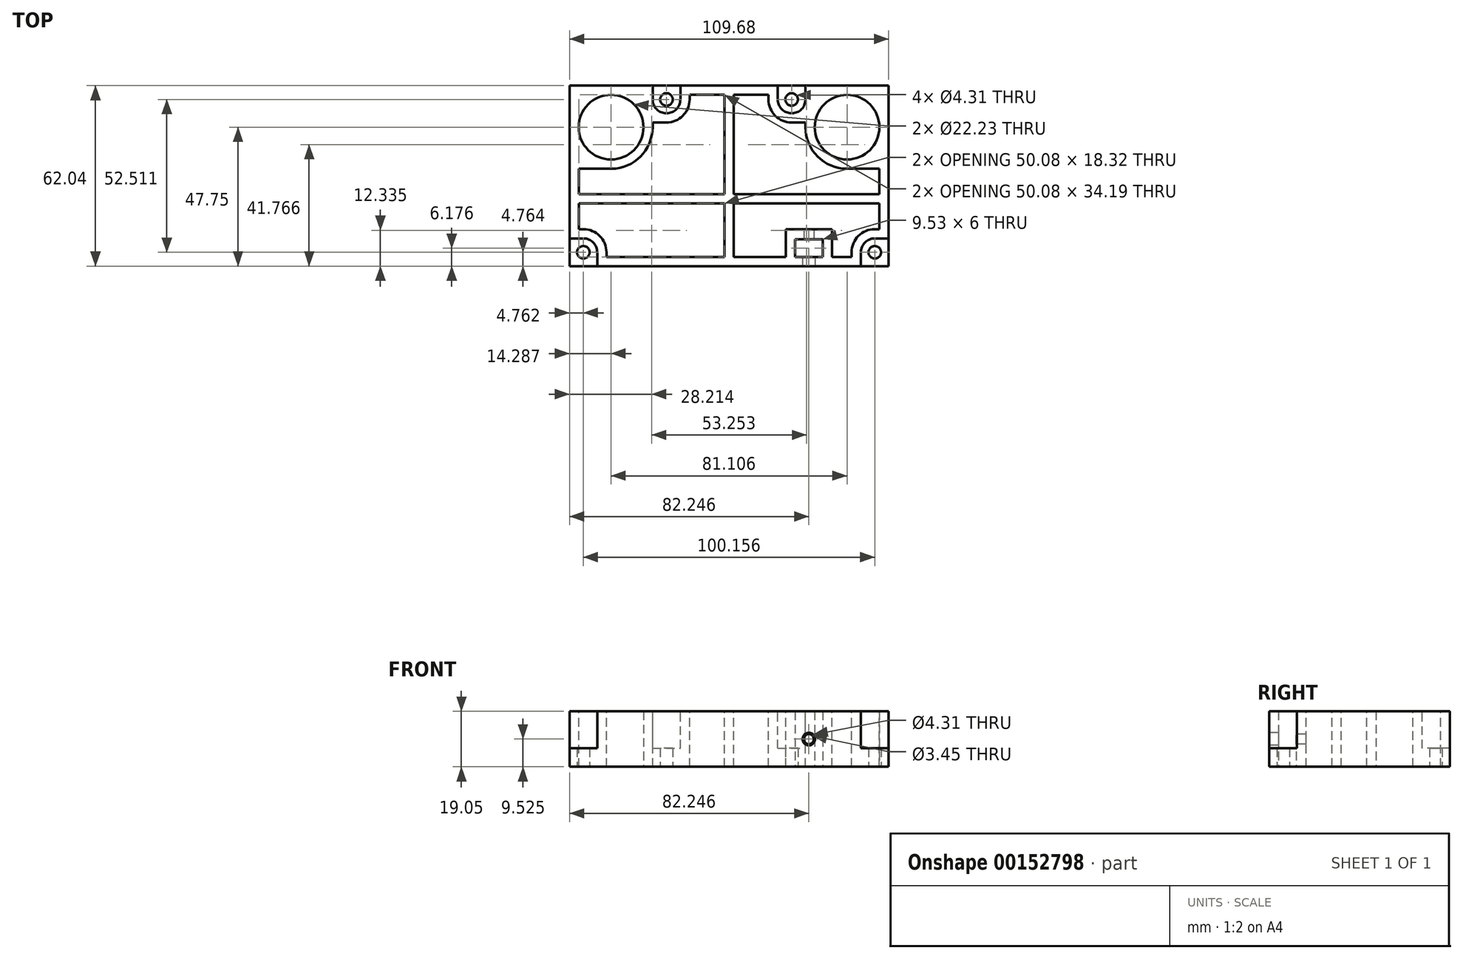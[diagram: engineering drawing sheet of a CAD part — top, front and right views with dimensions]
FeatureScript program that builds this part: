
annotation { "Feature Type Name" : "Feature", "Feature Type Description" : "" }
export const myFeature = defineFeature(function(context is Context, id is Id, definition is map)
    precondition{}
    {
        {
            var Q0;
            Q0=qCreatedBy(makeId("Top.planeOp"),FACE);
            var sketch = newSketch(context, id + "F0", { "sketchPlane" : qUnion([Q0])});
            skLineSegment(sketch, "E0.bottom", {"start": v(-40.55, 0) * mm, "end": v(40.55, 0) * mm, "construction": true});
            skPoint(sketch, "E0.middle", {"position": v(0, 0) * mm});
            skLineSegment(sketch, "E1", {"start": v(-40.55, 0) * mm, "end": v(-40.55, 14.29) * mm, "construction": true});
            skLineSegment(sketch, "E2", {"start": v(-40.55, 0) * mm, "end": v(-54.84, 0) * mm, "construction": true});
            skCircle(sketch, "E3", {"center": v(-40.55, 0) * mm, "radius": 11.11 * mm});
            skCircle(sketch, "E4", {"center": v(40.55, 0) * mm, "radius": 11.11 * mm});
            skLineSegment(sketch, "E5.bottom", {"start": v(-54.84, 14.29) * mm, "end": v(54.84, 14.29) * mm});
            skLineSegment(sketch, "E5.top", {"start": v(-54.84, -47.75) * mm, "end": v(54.84, -47.75) * mm});
            skLineSegment(sketch, "E5.left", {"start": v(-54.84, 14.29) * mm, "end": v(-54.84, -47.75) * mm});
            skLineSegment(sketch, "E5.right", {"start": v(54.84, 14.29) * mm, "end": v(54.84, -47.75) * mm});
            skLineSegment(sketch, "E6", {"start": v(0, 0) * mm, "end": v(0, -41.57) * mm, "construction": true});
            skLineSegment(sketch, "E7", {"start": v(0, -41.57) * mm, "end": v(22.64, -41.57) * mm, "construction": true});
            skLineSegment(sketch, "E8.bottom", {"start": v(22.64, -38.57) * mm, "end": v(32.17, -38.57) * mm});
            skLineSegment(sketch, "E8.top", {"start": v(22.64, -44.57) * mm, "end": v(32.17, -44.57) * mm});
            skLineSegment(sketch, "E8.left", {"start": v(22.64, -38.57) * mm, "end": v(22.64, -44.57) * mm});
            skLineSegment(sketch, "E8.right", {"start": v(32.17, -38.57) * mm, "end": v(32.17, -44.57) * mm});
            skLineSegment(sketch, "E9", {"start": v(0, -41.57) * mm, "end": v(0, -47.75) * mm, "construction": true});
            skLineSegment(sketch, "E10", {"start": v(0, 0) * mm, "end": v(0, 9.53) * mm, "construction": true});
            skLineSegment(sketch, "E11", {"start": v(-21.5, 9.53) * mm, "end": v(21.5, 9.53) * mm, "construction": true});
            skLineSegment(sketch, "E12", {"start": v(-50.08, -47.75) * mm, "end": v(-50.08, -42.99) * mm, "construction": true});
            skLineSegment(sketch, "E13", {"start": v(-50.08, -42.99) * mm, "end": v(-54.84, -42.99) * mm, "construction": true});
            skLineSegment(sketch, "E14", {"start": v(54.84, -42.99) * mm, "end": v(50.08, -42.99) * mm, "construction": true});
            skCircle(sketch, "E15", {"center": v(-50.08, -42.99) * mm, "radius": 2.15 * mm});
            skCircle(sketch, "E16", {"center": v(50.08, -42.99) * mm, "radius": 2.15 * mm});
            skCircle(sketch, "E17", {"center": v(-21.5, 9.53) * mm, "radius": 2.15 * mm});
            skCircle(sketch, "E18", {"center": v(21.5, 9.53) * mm, "radius": 2.15 * mm});
            skSolve(sketch);
        }
        {
            var Q0;
            Q0 = qSketchRegion(id + "F0", true);
            extrude(context, id + "F1", {"entities" : qUnion([Q0]), "depth" : 19.05 * mm});
        }
        {
            var Q0;
            Q0=makeQuery(id+"F1.opExtrude","CAP_FACE",FACE,{"disambiguationData":[OSD([sQuery(id+"F0.wireOp",EDGE,"E3"),sQuery(id+"F0.wireOp",EDGE,"E4"),sQuery(id+"F0.wireOp",EDGE,"E5.bottom"),sQuery(id+"F0.wireOp",EDGE,"E5.top"),sQuery(id+"F0.wireOp",EDGE,"E5.left"),sQuery(id+"F0.wireOp",EDGE,"E5.right"),sQuery(id+"F0.wireOp",EDGE,"E8.bottom"),sQuery(id+"F0.wireOp",EDGE,"E8.top"),sQuery(id+"F0.wireOp",EDGE,"E8.left"),sQuery(id+"F0.wireOp",EDGE,"E8.right"),sQuery(id+"F0.wireOp",EDGE,"E15"),sQuery(id+"F0.wireOp",EDGE,"E16"),sQuery(id+"F0.wireOp",EDGE,"E17"),sQuery(id+"F0.wireOp",EDGE,"E18")])],"isStart":false});
            var sketch = newSketch(context, id + "F2", { "sketchPlane" : qUnion([Q0])});
            skLineSegment(sketch, "E19.bottom", {"start": v(-26.27, 14.29) * mm, "end": v(-16.74, 14.29) * mm});
            skLineSegment(sketch, "E19.top", {"start": v(-26.27, 4.76) * mm, "end": v(-16.74, 4.76) * mm});
            skLineSegment(sketch, "E19.left", {"start": v(-26.27, 14.29) * mm, "end": v(-26.27, 4.76) * mm});
            skLineSegment(sketch, "E19.right", {"start": v(-16.74, 14.29) * mm, "end": v(-16.74, 4.76) * mm});
            skPoint(sketch, "E19.middle", {"position": v(-21.5, 9.53) * mm});
            skLineSegment(sketch, "E20.bottom", {"start": v(26.27, 14.29) * mm, "end": v(16.74, 14.29) * mm});
            skLineSegment(sketch, "E20.top", {"start": v(26.27, 4.76) * mm, "end": v(16.74, 4.76) * mm});
            skLineSegment(sketch, "E20.left", {"start": v(26.27, 14.29) * mm, "end": v(26.27, 4.76) * mm});
            skLineSegment(sketch, "E20.right", {"start": v(16.74, 14.29) * mm, "end": v(16.74, 4.76) * mm});
            skPoint(sketch, "E20.middle", {"position": v(21.5, 9.53) * mm});
            skLineSegment(sketch, "E21.bottom", {"start": v(54.84, -47.75) * mm, "end": v(45.32, -47.75) * mm});
            skLineSegment(sketch, "E21.top", {"start": v(54.84, -38.22) * mm, "end": v(45.32, -38.22) * mm});
            skLineSegment(sketch, "E21.left", {"start": v(54.84, -47.75) * mm, "end": v(54.84, -38.22) * mm});
            skLineSegment(sketch, "E21.right", {"start": v(45.32, -47.75) * mm, "end": v(45.32, -38.22) * mm});
            skPoint(sketch, "E21.middle", {"position": v(50.08, -42.99) * mm});
            skLineSegment(sketch, "E22.bottom", {"start": v(-54.84, -47.75) * mm, "end": v(-45.32, -47.75) * mm});
            skLineSegment(sketch, "E22.top", {"start": v(-54.84, -38.22) * mm, "end": v(-45.32, -38.22) * mm});
            skLineSegment(sketch, "E22.left", {"start": v(-54.84, -47.75) * mm, "end": v(-54.84, -38.22) * mm});
            skLineSegment(sketch, "E22.right", {"start": v(-45.32, -47.75) * mm, "end": v(-45.32, -38.22) * mm});
            skPoint(sketch, "E22.middle", {"position": v(-50.08, -42.99) * mm});
            skSolve(sketch);
        }
        {
            var Q0;
            Q0 = qSketchRegion(id + "F2", true);
            extrude(context, id + "F3", {"entities" : qUnion([Q0]), "operationType" : NewBodyOperationType.REMOVE, "oppositeDirection" : true, "depth" : 12.7 * mm});
        }
        {
            var Q0;
            Q0=makeQuery(id+"F3.boolean.opBoolean","COPY",EDGE,{"derivedFrom":makeQuery(id+"F3.opExtrude","SWEPT_EDGE",EDGE,{"disambiguationData":[OSD([sQuery(id+"F2.wireOp",EDGE,"E22.top"),sQuery(id+"F2.wireOp",EDGE,"E22.right")])]})});
            var Q1;
            Q1=makeQuery(id+"F3.boolean.opBoolean","COPY",EDGE,{"derivedFrom":makeQuery(id+"F3.opExtrude","SWEPT_EDGE",EDGE,{"disambiguationData":[OSD([sQuery(id+"F2.wireOp",EDGE,"E21.top"),sQuery(id+"F2.wireOp",EDGE,"E21.right")])]})});
            var Q2;
            Q2=makeQuery(id+"F3.boolean.opBoolean","COPY",EDGE,{"derivedFrom":makeQuery(id+"F3.opExtrude","SWEPT_EDGE",EDGE,{"disambiguationData":[OSD([sQuery(id+"F2.wireOp",EDGE,"E20.top"),sQuery(id+"F2.wireOp",EDGE,"E20.right")])]})});
            var Q3;
            Q3=makeQuery(id+"F3.boolean.opBoolean","COPY",EDGE,{"derivedFrom":makeQuery(id+"F3.opExtrude","SWEPT_EDGE",EDGE,{"disambiguationData":[OSD([sQuery(id+"F2.wireOp",EDGE,"E20.top"),sQuery(id+"F2.wireOp",EDGE,"E20.left")])]})});
            var Q4;
            Q4=makeQuery(id+"F3.boolean.opBoolean","COPY",EDGE,{"derivedFrom":makeQuery(id+"F3.opExtrude","SWEPT_EDGE",EDGE,{"disambiguationData":[OSD([sQuery(id+"F2.wireOp",EDGE,"E19.top"),sQuery(id+"F2.wireOp",EDGE,"E19.right")])]})});
            var Q5;
            Q5=makeQuery(id+"F3.boolean.opBoolean","COPY",EDGE,{"derivedFrom":makeQuery(id+"F3.opExtrude","SWEPT_EDGE",EDGE,{"disambiguationData":[OSD([sQuery(id+"F2.wireOp",EDGE,"E19.top"),sQuery(id+"F2.wireOp",EDGE,"E19.left")])]})});
            fillet(context, id + "F4", {"entities" : qUnion([Q0, Q1, Q2, Q3, Q4, Q5]), "radius" : 4.76 * mm, "tangentPropagation" : true, "allowEdgeOverflow" : false});
        }
        {
            var Q0;
            Q0=makeQuery(id+"F1.opExtrude","CAP_FACE",FACE,{"disambiguationData":[OSD([sQuery(id+"F0.wireOp",EDGE,"E3"),sQuery(id+"F0.wireOp",EDGE,"E4"),sQuery(id+"F0.wireOp",EDGE,"E5.bottom"),sQuery(id+"F0.wireOp",EDGE,"E5.top"),sQuery(id+"F0.wireOp",EDGE,"E5.left"),sQuery(id+"F0.wireOp",EDGE,"E5.right"),sQuery(id+"F0.wireOp",EDGE,"E8.bottom"),sQuery(id+"F0.wireOp",EDGE,"E8.top"),sQuery(id+"F0.wireOp",EDGE,"E8.left"),sQuery(id+"F0.wireOp",EDGE,"E8.right"),sQuery(id+"F0.wireOp",EDGE,"E15"),sQuery(id+"F0.wireOp",EDGE,"E16"),sQuery(id+"F0.wireOp",EDGE,"E17"),sQuery(id+"F0.wireOp",EDGE,"E18")])],"isStart":false});
            var sketch = newSketch(context, id + "F5", { "sketchPlane" : qUnion([Q0])});
            skLineSegment(sketch, "E23.bottom", {"start": v(51.67, -23.08) * mm, "end": v(-51.67, -23.08) * mm});
            skLineSegment(sketch, "E23.top", {"start": v(51.67, -26.26) * mm, "end": v(-51.67, -26.26) * mm});
            skLineSegment(sketch, "E23.left", {"start": v(51.67, -23.08) * mm, "end": v(51.67, -26.26) * mm, "construction": true});
            skLineSegment(sketch, "E23.right", {"start": v(-51.67, -23.08) * mm, "end": v(-51.67, -26.26) * mm, "construction": true});
            skLineSegment(sketch, "E24.bottom", {"start": v(-1.59, -44.57) * mm, "end": v(1.59, -44.57) * mm, "construction": true});
            skLineSegment(sketch, "E24.top", {"start": v(-1.59, 11.11) * mm, "end": v(1.59, 11.11) * mm, "construction": true});
            skLineSegment(sketch, "E24.left", {"start": v(-1.59, -44.57) * mm, "end": v(-1.59, 11.11) * mm});
            skLineSegment(sketch, "E24.right", {"start": v(1.59, -44.57) * mm, "end": v(1.59, 11.11) * mm});
            skArc(sketch, "E25", {"start": v(-40.55, -14.29) * mm, "mid": v(-30.45, -10.1) * mm, "end": v(-26.27, 0) * mm});
            skArc(sketch, "E26", {"start": v(-21.5, 1.59) * mm, "mid": v(-15.9, 3.91) * mm, "end": v(-13.57, 9.53) * mm});
            skArc(sketch, "E27", {"start": v(13.57, 9.53) * mm, "mid": v(15.9, 3.91) * mm, "end": v(21.5, 1.59) * mm});
            skArc(sketch, "E28", {"start": v(26.27, 0) * mm, "mid": v(30.45, -10.1) * mm, "end": v(40.55, -14.29) * mm});
            skArc(sketch, "E29", {"start": v(50.08, -35.05) * mm, "mid": v(44.47, -37.37) * mm, "end": v(42.14, -42.99) * mm});
            skArc(sketch, "E30", {"start": v(-42.14, -42.99) * mm, "mid": v(-44.47, -37.37) * mm, "end": v(-50.08, -35.05) * mm});
            skLineSegment(sketch, "E31", {"start": v(27.4, -44.57) * mm, "end": v(27.4, -47.75) * mm, "construction": true});
            skLineSegment(sketch, "E32", {"start": v(27.4, -44.57) * mm, "end": v(27.4, -35.05) * mm, "construction": true});
            skLineSegment(sketch, "E33.bottom", {"start": v(19.47, -35.05) * mm, "end": v(35.34, -35.05) * mm});
            skLineSegment(sketch, "E33.left", {"start": v(19.47, -35.05) * mm, "end": v(19.47, -44.57) * mm});
            skLineSegment(sketch, "E33.right", {"start": v(35.34, -35.05) * mm, "end": v(35.34, -44.57) * mm});
            skLineSegment(sketch, "E34", {"start": v(22.64, -38.57) * mm, "end": v(19.47, -38.57) * mm, "construction": true});
            skLineSegment(sketch, "E35", {"start": v(19.47, -44.57) * mm, "end": v(1.59, -44.57) * mm});
            skLineSegment(sketch, "E36", {"start": v(35.34, -44.57) * mm, "end": v(42.14, -44.57) * mm});
            skLineSegment(sketch, "E37", {"start": v(42.14, -44.57) * mm, "end": v(42.14, -42.99) * mm});
            skLineSegment(sketch, "E38", {"start": v(-1.59, -44.57) * mm, "end": v(-42.14, -44.57) * mm});
            skLineSegment(sketch, "E39", {"start": v(0, -44.57) * mm, "end": v(0, -47.75) * mm, "construction": true});
            skLineSegment(sketch, "E40", {"start": v(-42.14, -44.57) * mm, "end": v(-42.14, -42.99) * mm});
            skLineSegment(sketch, "E41", {"start": v(-40.55, -14.29) * mm, "end": v(-51.67, -14.29) * mm});
            skLineSegment(sketch, "E42", {"start": v(-51.67, -14.29) * mm, "end": v(-51.67, -23.08) * mm});
            skLineSegment(sketch, "E43", {"start": v(-50.08, -35.05) * mm, "end": v(-51.67, -35.05) * mm});
            skLineSegment(sketch, "E44", {"start": v(-51.67, -35.05) * mm, "end": v(-51.67, -26.26) * mm});
            skLineSegment(sketch, "E45", {"start": v(-51.67, -14.29) * mm, "end": v(-54.84, -14.29) * mm, "construction": true});
            skLineSegment(sketch, "E46", {"start": v(-26.27, 0) * mm, "end": v(-26.27, 1.59) * mm});
            skLineSegment(sketch, "E47", {"start": v(-26.27, 1.59) * mm, "end": v(-21.5, 1.59) * mm});
            skLineSegment(sketch, "E48", {"start": v(50.08, -35.05) * mm, "end": v(51.67, -35.05) * mm});
            skLineSegment(sketch, "E49", {"start": v(51.67, -35.05) * mm, "end": v(51.67, -26.26) * mm});
            skLineSegment(sketch, "E50", {"start": v(51.67, -23.08) * mm, "end": v(51.67, -14.29) * mm});
            skLineSegment(sketch, "E51", {"start": v(51.67, -14.29) * mm, "end": v(40.55, -14.29) * mm});
            skLineSegment(sketch, "E52", {"start": v(26.27, 0) * mm, "end": v(26.27, 1.59) * mm});
            skLineSegment(sketch, "E53", {"start": v(26.27, 1.59) * mm, "end": v(21.5, 1.59) * mm});
            skLineSegment(sketch, "E54", {"start": v(-13.57, 9.53) * mm, "end": v(-13.57, 11.11) * mm});
            skLineSegment(sketch, "E55", {"start": v(-13.57, 11.11) * mm, "end": v(-1.59, 11.11) * mm});
            skLineSegment(sketch, "E56", {"start": v(13.57, 9.53) * mm, "end": v(13.57, 11.11) * mm});
            skLineSegment(sketch, "E57", {"start": v(13.57, 11.11) * mm, "end": v(1.59, 11.11) * mm});
            skLineSegment(sketch, "E58", {"start": v(0, 11.11) * mm, "end": v(0, 14.29) * mm, "construction": true});
            skLineSegment(sketch, "E59", {"start": v(51.67, -24.67) * mm, "end": v(54.84, -24.67) * mm, "construction": true});
            skSolve(sketch);
        }
        {
            var Q0;
            Q0=makeQuery(id+"F5.imprint","IMPRINT",FACE,{"disambiguationData":[TD([[makeQuery(id+"F5.imprint","IMPRINT",EDGE,{"derivedFrom":sQuery(id+"F5.wireOp",EDGE,"E25")}),-1.0]])]});
            var Q1;
            Q1=makeQuery(id+"F5.imprint","IMPRINT",FACE,{"disambiguationData":[TD([[makeQuery(id+"F5.imprint","IMPRINT",EDGE,{"derivedFrom":sQuery(id+"F5.wireOp",EDGE,"E30")}),-1.0]])]});
            var Q2;
            Q2=makeQuery(id+"F5.imprint","IMPRINT",FACE,{"disambiguationData":[TD([[makeQuery(id+"F5.imprint","IMPRINT",EDGE,{"derivedFrom":sQuery(id+"F5.wireOp",EDGE,"E27")}),-1.0]])]});
            var Q3;
            Q3=makeQuery(id+"F5.imprint","IMPRINT",FACE,{"disambiguationData":[TD([[makeQuery(id+"F5.imprint","IMPRINT",EDGE,{"derivedFrom":sQuery(id+"F5.wireOp",EDGE,"E29")}),-1.0]])]});
            var Q4;
            Q4=makeQuery(id+"F1.opExtrude","CAP_FACE",FACE,{"disambiguationData":[OSD([sQuery(id+"F0.wireOp",EDGE,"E3"),sQuery(id+"F0.wireOp",EDGE,"E4"),sQuery(id+"F0.wireOp",EDGE,"E5.bottom"),sQuery(id+"F0.wireOp",EDGE,"E5.top"),sQuery(id+"F0.wireOp",EDGE,"E5.left"),sQuery(id+"F0.wireOp",EDGE,"E5.right"),sQuery(id+"F0.wireOp",EDGE,"E8.bottom"),sQuery(id+"F0.wireOp",EDGE,"E8.top"),sQuery(id+"F0.wireOp",EDGE,"E8.left"),sQuery(id+"F0.wireOp",EDGE,"E8.right"),sQuery(id+"F0.wireOp",EDGE,"E15"),sQuery(id+"F0.wireOp",EDGE,"E16"),sQuery(id+"F0.wireOp",EDGE,"E17"),sQuery(id+"F0.wireOp",EDGE,"E18")])],"isStart":true});
            extrude(context, id + "F6", {"entities" : qUnion([Q0, Q1, Q2, Q3]), "operationType" : NewBodyOperationType.REMOVE, "endBound" : BoundingType.UP_TO_SURFACE, "oppositeDirection" : true, "endBoundEntityFace" : qUnion([Q4]), "depth" : 25.4 * mm});
        }
        {
            var Q0;
            Q0=makeQuery(id+"F1.opExtrude","SWEPT_FACE",FACE,{"disambiguationData":[OSD([sQuery(id+"F0.wireOp",EDGE,"E5.top")])]});
            var sketch = newSketch(context, id + "F7", { "sketchPlane" : qUnion([Q0])});
            skLineSegment(sketch, "E60", {"start": v(27.4, 19.05) * mm, "end": v(27.4, 0) * mm, "construction": true});
            skCircle(sketch, "E61", {"center": v(27.4, 9.53) * mm, "radius": 2.15 * mm});
            skSolve(sketch);
        }
        {
            var Q0;
            Q0 = qSketchRegion(id + "F7", true);
            var Q1;
            Q1=makeQuery(id+"F1.opExtrude","SWEPT_FACE",FACE,{"disambiguationData":[OSD([sQuery(id+"F0.wireOp",EDGE,"E8.top")])]});
            extrude(context, id + "F8", {"entities" : qUnion([Q0]), "operationType" : NewBodyOperationType.REMOVE, "endBound" : BoundingType.UP_TO_SURFACE, "oppositeDirection" : true, "endBoundEntityFace" : qUnion([Q1]), "depth" : 25.4 * mm});
        }
        {
            var Q0;
            Q0=makeQuery(id+"F1.opExtrude","SWEPT_FACE",FACE,{"disambiguationData":[OSD([sQuery(id+"F0.wireOp",EDGE,"E8.bottom")])]});
            var sketch = newSketch(context, id + "F9", { "sketchPlane" : qUnion([Q0])});
            skCircle(sketch, "E62", {"center": v(27.4, 9.53) * mm, "radius": 1.73 * mm});
            skSolve(sketch);
        }
        {
            var Q0;
            Q0 = qSketchRegion(id + "F9", true);
            var Q1;
            Q1=makeQuery(id+"F6.boolean.opBoolean","COPY",FACE,{"derivedFrom":makeQuery(id+"F6.opExtrude","SWEPT_FACE",FACE,{"disambiguationData":[OSD([sQuery(id+"F5.wireOp",EDGE,"E33.bottom")])]})});
            extrude(context, id + "F10", {"entities" : qUnion([Q0]), "operationType" : NewBodyOperationType.REMOVE, "endBound" : BoundingType.UP_TO_SURFACE, "oppositeDirection" : true, "endBoundEntityFace" : qUnion([Q1]), "depth" : 25.4 * mm});
        }
    });
